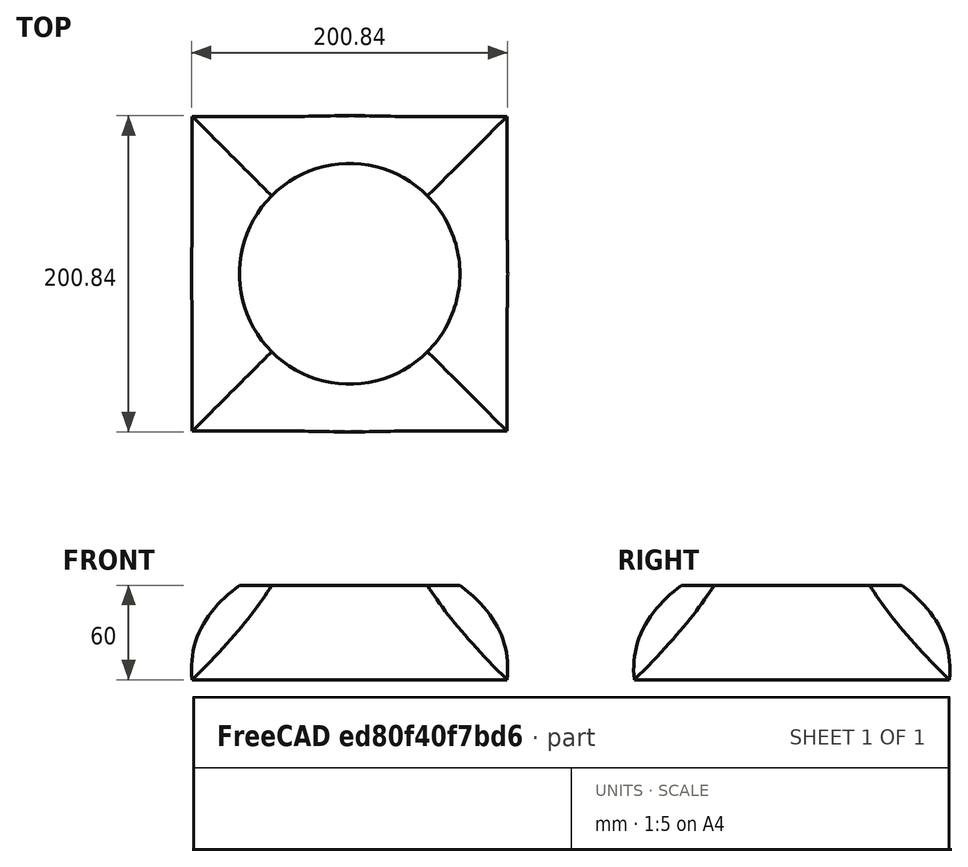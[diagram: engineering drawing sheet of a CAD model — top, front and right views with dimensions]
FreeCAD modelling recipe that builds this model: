
FCSTD DOCUMENT  (FreeCAD 0.15R4671 (Git))
Label: mark3
License: All rights reserved
LicenseURL: http://en.wikipedia.org/wiki/All_rights_reserved
objects: Sketcher::SketchObject×3, Part::Loft×1
note: 4 computed .brp shape members not serialized (recipe doc carries the construction recipe); baked Part::Feature solids carry a one-line shape summary decoded from their .brp

FEATURE [Sketcher::SketchObject] Sketch  label="kuklos"
  sketch-geometry (1):
    g0: Circle CenterX=0 CenterY=0 CenterZ=0 NormalX=0 NormalY=0 NormalZ=1 Radius=70
  constraints (2):
    c: Coincident(g0,g-1)
    c: Radius(g0) = 70
FEATURE [Sketcher::SketchObject] Sketch001  label="kuklos2"
  Placement = pos=(0,0,-20) rot=(0,0,1;0rad)
  sketch-geometry (1):
    g0: Circle CenterX=0 CenterY=0 CenterZ=0 NormalX=0 NormalY=0 NormalZ=1 Radius=90
  constraints (2):
    c: Coincident(g0,g-1)
    c: Radius(g0) = 90
FEATURE [Sketcher::SketchObject] Sketch002  label="tetragwno"
  Placement = pos=(0,0,-60) rot=(0,0,1;0rad)
  sketch-geometry (4):
    g0: LineSegment StartX=-100 StartY=100 StartZ=0 EndX=100 EndY=100 EndZ=0
    g1: LineSegment StartX=100 StartY=100 StartZ=0 EndX=100 EndY=-100 EndZ=0
    g2: LineSegment StartX=100 StartY=-100 StartZ=0 EndX=-100 EndY=-100 EndZ=0
    g3: LineSegment StartX=-100 StartY=-100 StartZ=0 EndX=-100 EndY=100 EndZ=0
  constraints (12):
    c: Coincident(g0,g1)
    c: Coincident(g1,g2)
    c: Coincident(g2,g3)
    c: Coincident(g3,g0)
    c: Horizontal(g0)
    c: Horizontal(g2)
    c: Vertical(g1)
    c: Vertical(g3)
    c: Equal(g0,g3)
    c: Symmetric(g0,g0,g-2)
    c: Symmetric(g0,g2,g-1)
    c: DistanceY(g3) = 200
FEATURE [Part::Loft] Loft
  Closed = false
  Ruled = false
  Sections = -> [Sketch002,Sketch001,Sketch]
  Solid = false
